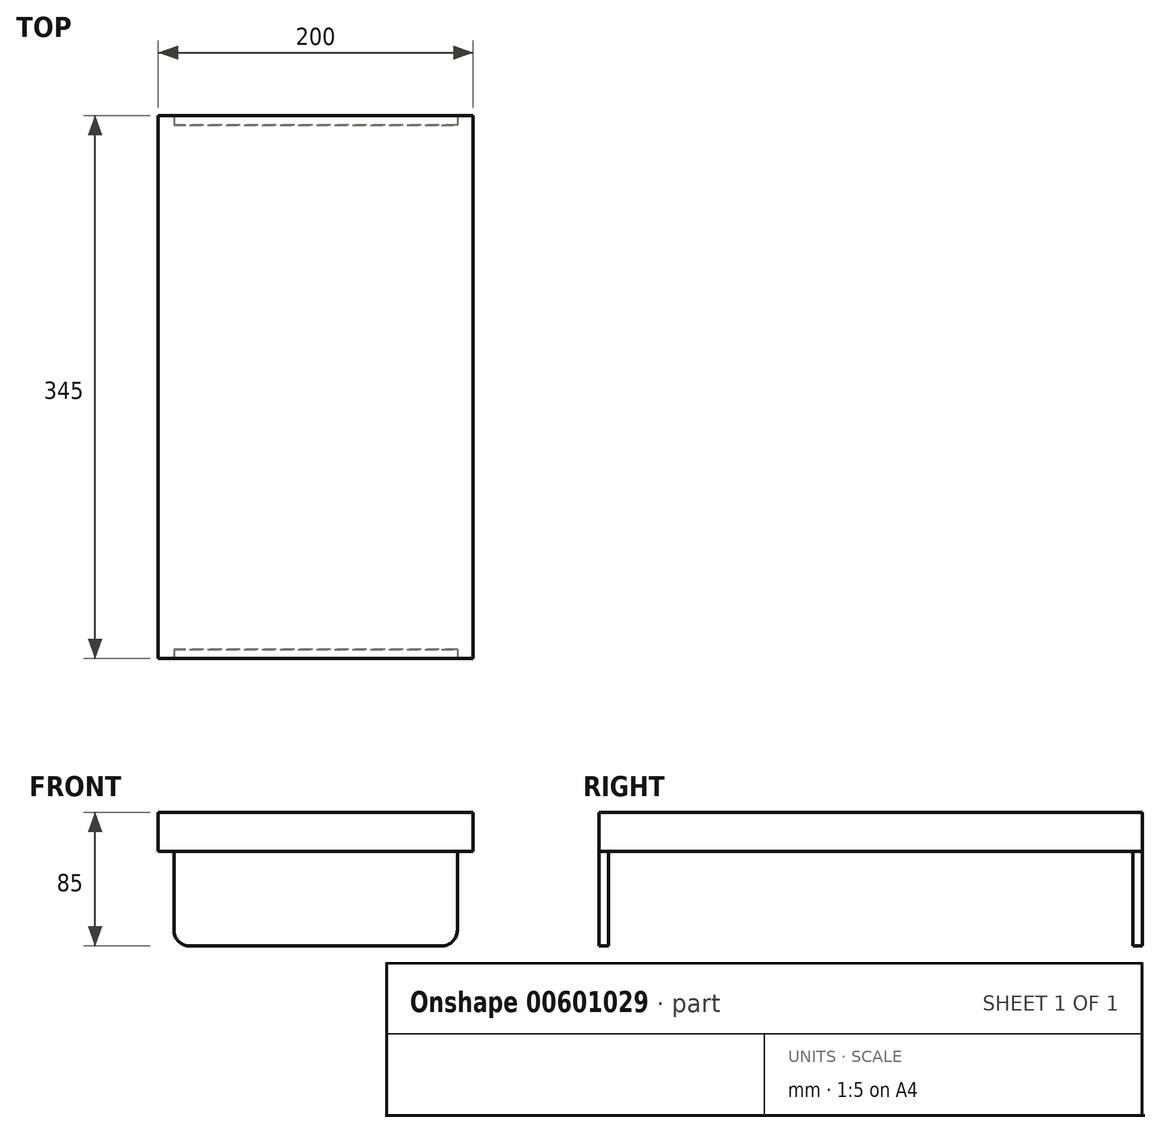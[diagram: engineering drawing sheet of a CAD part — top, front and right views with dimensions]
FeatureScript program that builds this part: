
annotation { "Feature Type Name" : "Feature", "Feature Type Description" : "" }
export const myFeature = defineFeature(function(context is Context, id is Id, definition is map)
    precondition{}
    {
        {
            var Q0;
            Q0=qCreatedBy(makeId("Top.planeOp"),FACE);
            var sketch = newSketch(context, id + "F0", { "sketchPlane" : qUnion([Q0])});
            skLineSegment(sketch, "E0.bottom", {"start": v(100, -172.5) * mm, "end": v(-100, -172.5) * mm});
            skLineSegment(sketch, "E0.top", {"start": v(100, 172.5) * mm, "end": v(-100, 172.5) * mm});
            skLineSegment(sketch, "E0.left", {"start": v(100, -172.5) * mm, "end": v(100, 172.5) * mm});
            skLineSegment(sketch, "E0.right", {"start": v(-100, -172.5) * mm, "end": v(-100, 172.5) * mm});
            skPoint(sketch, "E0.middle", {"position": v(0, 0) * mm});
            skSolve(sketch);
        }
        {
            var Q0;
            Q0 = qSketchRegion(id + "F0", true);
            extrude(context, id + "F1", {"entities" : qUnion([Q0]), "depth" : 25 * mm, "offsetDistance" : 25 * mm});
        }
        {
            var Q0;
            Q0=makeQuery(id+"F1.opExtrude","SWEPT_FACE",FACE,{"disambiguationData":[OSD([sQuery(id+"F0.wireOp",EDGE,"E0.bottom")])]});
            var sketch = newSketch(context, id + "F2", { "sketchPlane" : qUnion([Q0])});
            skLineSegment(sketch, "E1.bottom", {"start": v(-90, 0) * mm, "end": v(90, 0) * mm});
            skLineSegment(sketch, "E1.top", {"start": v(-80, -60) * mm, "end": v(80, -60) * mm});
            skLineSegment(sketch, "E1.left", {"start": v(-90, 0) * mm, "end": v(-90, -50) * mm});
            skLineSegment(sketch, "E1.right", {"start": v(90, 0) * mm, "end": v(90, -50) * mm});
            skPoint(sketch, "E2.visualSharp", {"position": v(-90, -60) * mm});
            skArc(sketch, "E2.filletArc", {"start": v(-90, -50) * mm, "mid": v(-87.07, -57.07) * mm, "end": v(-80, -60) * mm});
            skPoint(sketch, "E3.visualSharp", {"position": v(90, -60) * mm});
            skArc(sketch, "E3.filletArc", {"start": v(80, -60) * mm, "mid": v(87.07, -57.07) * mm, "end": v(90, -50) * mm});
            skSolve(sketch);
        }
        {
            var Q0;
            Q0 = qSketchRegion(id + "F2", true);
            extrude(context, id + "F3", {"entities" : qUnion([Q0]), "oppositeDirection" : true, "depth" : 6 * mm, "offsetDistance" : 25 * mm});
        }
        {
            var Q0;
            Q0=makeQuery(id+"F3.opExtrude","SWEPT_BODY",BODY,{"disambiguationData":[OSD([sQuery(id+"F2.wireOp",EDGE,"E1.bottom"),sQuery(id+"F2.wireOp",EDGE,"E1.top"),sQuery(id+"F2.wireOp",EDGE,"E1.left"),sQuery(id+"F2.wireOp",EDGE,"E1.right"),sQuery(id+"F2.wireOp",EDGE,"E2.filletArc"),sQuery(id+"F2.wireOp",EDGE,"E3.filletArc")])]});
            transform(context, id + "F4", {"entities" : qUnion([Q0]), "transformType" : TransformType.TRANSLATION_3D, "dx" : 0 * mm, "dy" : 339 * mm, "dz" : 0 * mm, "makeCopy" : true});
        }
    });
